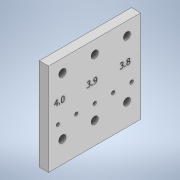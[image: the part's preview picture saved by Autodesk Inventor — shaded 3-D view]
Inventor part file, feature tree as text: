
AUTODESK INVENTOR PART (.ipt)
format: ipt  version: 2021 (Build 250183000, 183)  size: 488,960 bytes
history: native  units: mm
features: hole x8, sketch x4, extrude x1, emboss x1, projected_geometry x1
ambient origin geometry x8: Origin, YZ Plane, XZ Plane, XY Plane, X Axis, Y Axis, Z Axis, Center Point
bodies: Solid1 (feature_tree)
feature tree (15):
  extrude  "Extrusion1"  Depth=50.0mm
  sketch  "Sketch2"  dims[d2=5.0mm d3=0.0mm d4=7.5mm]
  hole  "Hole1"  [1 undecoded]
  hole  "Hole2"  [1 undecoded]
  hole  "Hole3"  [1 undecoded]
  emboss  "Emboss1"
  sketch  "Sketch4"  dims[d7=12.0mm d8=12.0mm d9=31.0mm d10=31.0mm d11=31.0mm d12=4.0mm d13=6.0mm d14=4.0mm d15=2.0mm d16=90.0deg d17=8.0mm d18=20.594885mm d19=3.9mm d20=6.0mm d21=4.0mm d22=2.0mm d23=90.0deg d24=8.0mm d25=20.594885mm d26=3.8mm d27=6.0mm d28=4.0mm d29=2.0mm d30=90.0deg d31=8.0mm d32=20.594885mm d33=1.0mm d34=0.0mm d35=20.0mm d36=20.0mm d37=40.0mm d38=1.75mm d39=6.0mm d40=4.0mm d41=2.0mm d42=90.0deg d43=8.0mm d44=20.594885mm d45=1.8mm d46=6.0mm d47=4.0mm d48=2.0mm d49=90.0deg d50=8.0mm d51=20.594885mm d52=1.85mm d53=6.0mm d54=4.0mm d55=2.0mm d56=90.0deg d57=8.0mm d58=20.594885mm d59=1.9mm d60=6.0mm d61=4.0mm d62=2.0mm d63=90.0deg d64=8.0mm d65=20.594885mm d66=1.95mm d67=6.0mm d68=4.0mm d69=2.0mm d70=90.0deg d71=8.0mm d72=20.594885mm]
  hole  "Hole4"  [1 undecoded]
  hole  "Hole5"  [1 undecoded]
  hole  "Hole6"  [1 undecoded]
  hole  "Hole7"  [1 undecoded]
  hole  "Hole8"  [1 undecoded]
  sketch  "Sketch1"  dims[d0=50.0mm d1=50.0mm]
  sketch  "Sketch3"  dims[d5=7.5mm d6=12.0mm]
  projected_geometry  "Projected Loop1"
note: 8 required parameter values undecoded (feature->parameter linkage not recoverable at this tier; creation-order binding heuristic only, values carry confidence <= 0.55)
